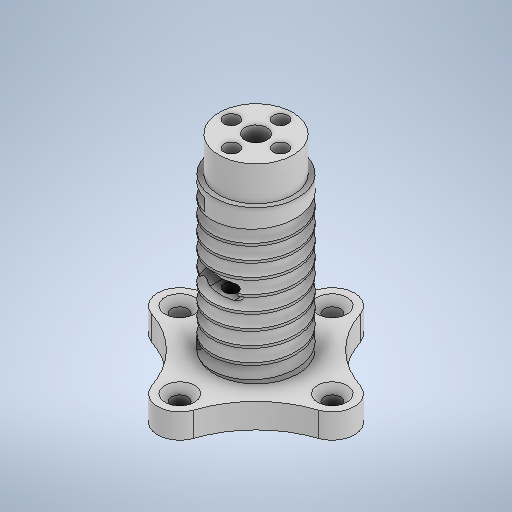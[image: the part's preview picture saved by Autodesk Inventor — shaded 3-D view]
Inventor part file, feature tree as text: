
AUTODESK INVENTOR PART (.ipt)
format: ipt  version: 2025.2 (Build 292293000, 293)  size: 1,189,888 bytes
history: native  units: mm
features: sketch x15, extrude x11, projected_geometry x2, plane x1, helix x1, chamfer x1, other x1
ambient origin geometry x8: Origin, YZ Plane, XZ Plane, XY Plane, X Axis, Y Axis, Z Axis, Center Point
bodies: Solid1 (feature_tree)
feature tree (32):
  extrude  "Extrusion1"  Depth=9.0mm
  extrude  "Extrusion2"  Depth=9.0mm
  extrude  "Extrusion3"  Depth=31.0mm
  plane  "Work Plane1"
  helix  "Coil2"  [1 undecoded]
  extrude  "Extrusion4"  Depth=20.0mm
  extrude  "Extrusion5"  Depth=20.0mm
  extrude  "Extrusion6"  Depth=5.0mm TaperAngle=0.0deg
  extrude  "Extrusion7"  Depth=38.0mm TaperAngle=0.0deg
  extrude  "Extrusion8"  Depth=7.0mm TaperAngle=0.0deg
  chamfer  "Chamfer1"  Distance=3.0mm
  extrude  "Extrusion9"  Depth=5.0mm
  extrude  "Extrusion10"  TaperAngle=0.0deg  [1 undecoded]
  extrude  "Extrusion11"  Depth=0.2mm
  sketch  "Sketch1"  dims[d0=9.0mm d1=9.0mm]
  sketch  "Sketch2"  dims[d5=31.0mm d6=31.0mm d10=15.5mm]
  sketch  "Sketch3"  dims[d13=20.0mm d14=20.0mm]
  other  "Work Axis2"
  sketch  "Sketch6"  dims[d18=17.0mm d19=38.0mm d20=0.0mm]
  sketch  "Sketch7"  dims[d21=15.0mm d22=7.0mm d23=0.0mm]
  sketch  "Sketch8"  dims[d33=135.0deg]
  sketch  "Sketch Circular Pattern1"  dims[d2=9.0mm d3=9.0mm]
  sketch  "Sketch9"  dims[d34=2.5mm]
  sketch  "Sketch Circular Pattern2"  dims[d11=15.5mm d12=20.0mm]
  sketch  "Sketch10"  dims[d35=3.0mm d36=27.25mm d37=80.0mm d38=0.0mm d39=90.0deg d40=90.0deg d41=0.0mm d42=0.0mm]
  sketch  "Sketch11"  dims[d45=5.0mm]
  sketch  "Sketch Circular Pattern3"  dims[d15=20.0mm d16=5.0mm d17=0.0mm]
  sketch  "Sketch12"  dims[d46=1.5mm]
  sketch  "Sketch15"  dims[d47=1.5mm]
  projected_geometry  "Projected Loop2"
  sketch  "Sketch16"  dims[d49=14.875mm d50=3.0mm d51=5.0mm d52=0.0mm d53=0.0mm d54=4.5mm d55=5.5mm d56=40.0mm d58=360.0deg d60=4.0mm d61=4.0mm d62=4.0mm d63=4.0mm d64=3.5mm d65=0.0mm d66=3.0mm d67=40.0mm d69=360.0deg d71=0.0mm d72=0.0mm d73=4.5mm d74=4.0mm d75=0.0mm d76=3.3mm d77=40.0mm d79=360.0deg d81=0.0mm d82=0.0mm d83=1.35mm d84=2.0mm d85=45.0deg d86=4.45mm d87=7.5mm d88=0.0mm d90=0.2mm d91=0.0mm d92=0.2mm d93=0.0mm d89=0.5mm d94=0.5mm d95=0.872665mm]
  projected_geometry  "Projected Loop3"
note: 2 required parameter values undecoded (feature->parameter linkage not recoverable at this tier; creation-order binding heuristic only, values carry confidence <= 0.55)
